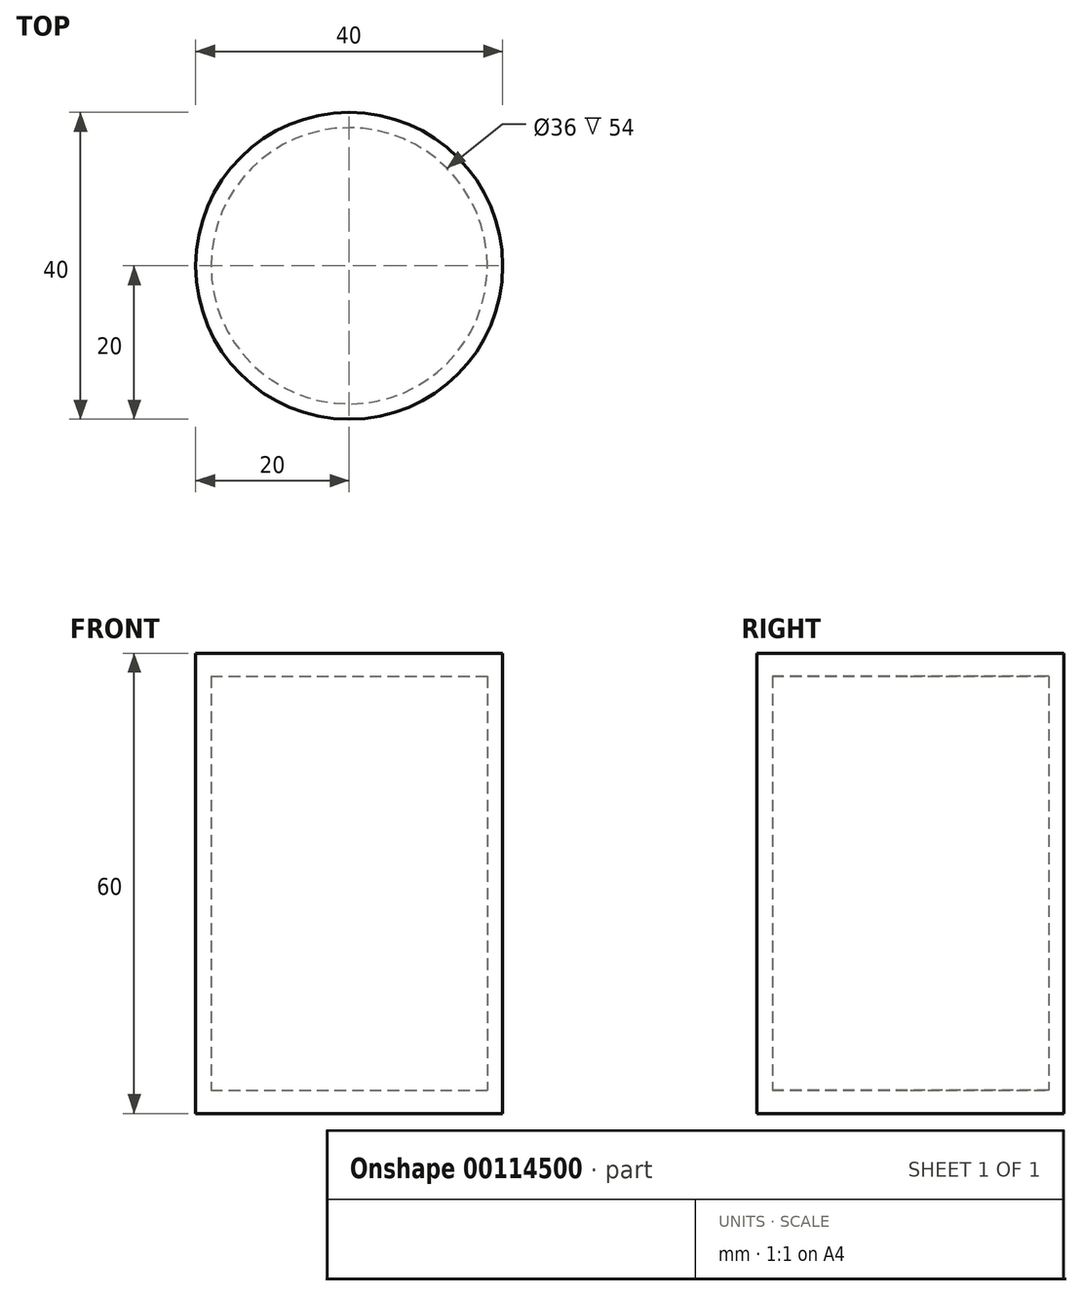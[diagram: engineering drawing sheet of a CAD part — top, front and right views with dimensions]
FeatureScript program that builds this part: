
annotation { "Feature Type Name" : "Feature", "Feature Type Description" : "" }
export const myFeature = defineFeature(function(context is Context, id is Id, definition is map)
    precondition{}
    {
        {
            var Q0;
            Q0=qCreatedBy(makeId("Front.planeOp"),FACE);
            var sketch = newSketch(context, id + "F0", { "sketchPlane" : qUnion([Q0])});
            skLineSegment(sketch, "E0", {"start": v(0, 60) * mm, "end": v(-20, 60) * mm});
            skLineSegment(sketch, "E1", {"start": v(-20, 60) * mm, "end": v(-20, 0) * mm});
            skLineSegment(sketch, "E2", {"start": v(-20, 0) * mm, "end": v(0, 0) * mm});
            skLineSegment(sketch, "E3", {"start": v(0, 0) * mm, "end": v(0, 3) * mm});
            skLineSegment(sketch, "E4", {"start": v(0, 3) * mm, "end": v(-18, 3) * mm});
            skLineSegment(sketch, "E5", {"start": v(-18, 3) * mm, "end": v(-18, 57) * mm});
            skLineSegment(sketch, "E6", {"start": v(-18, 57) * mm, "end": v(0, 57) * mm});
            skLineSegment(sketch, "E7", {"start": v(0, 57) * mm, "end": v(0, 60) * mm});
            skLineSegment(sketch, "E8", {"start": v(0, 0) * mm, "end": v(0, 60) * mm, "construction": true});
            skSolve(sketch);
        }
        {
            var Q0;
            Q0=makeQuery(id+"F0.imprint","IMPRINT",FACE,{"disambiguationData":[TD([[makeQuery(id+"F0.imprint","IMPRINT",EDGE,{"derivedFrom":sQuery(id+"F0.wireOp",EDGE,"E0")}),1.0]])]});
            var Q1;
            Q1=sQuery(id+"F0.wireOp",EDGE,"E8");
            revolve(context, id + "F1", {"entities" : qUnion([Q0]), "axis" : qUnion([Q1]), "revolveType" : RevolveType.FULL});
        }
    });
